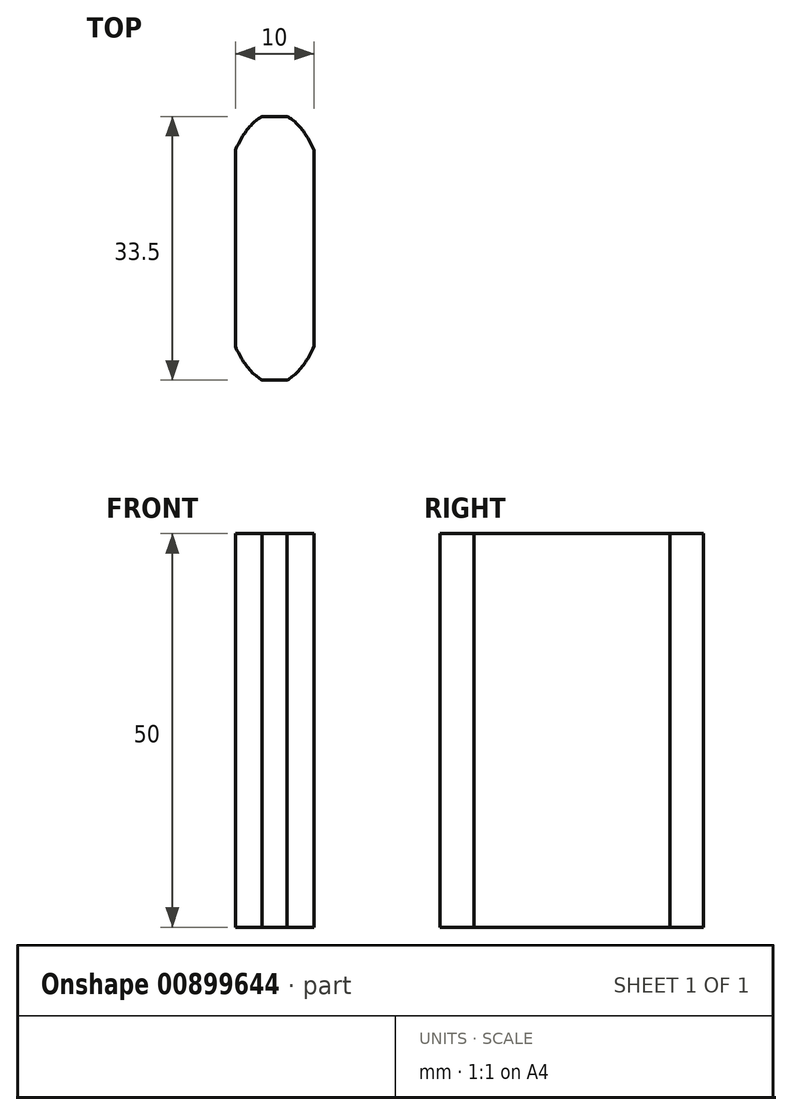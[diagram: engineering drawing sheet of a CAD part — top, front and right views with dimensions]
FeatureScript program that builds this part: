
annotation { "Feature Type Name" : "Feature", "Feature Type Description" : "" }
export const myFeature = defineFeature(function(context is Context, id is Id, definition is map)
    precondition{}
    {
        {
            var Q0;
            Q0=qCreatedBy(makeId("Right.planeOp"),FACE);
            var sketch = newSketch(context, id + "F0", { "sketchPlane" : qUnion([Q0])});
            skLineSegment(sketch, "E0.bottom", {"start": v(-36.1, 65.33) * mm, "end": v(-2.6, 65.33) * mm});
            skLineSegment(sketch, "E0.top", {"start": v(-36.1, 15.33) * mm, "end": v(-2.6, 15.33) * mm});
            skLineSegment(sketch, "E0.left", {"start": v(-36.1, 65.33) * mm, "end": v(-36.1, 15.33) * mm});
            skLineSegment(sketch, "E0.right", {"start": v(-2.6, 65.33) * mm, "end": v(-2.6, 15.33) * mm});
            skSolve(sketch);
        }
        {
            var Q0;
            Q0=makeQuery(id+"F0.imprint","IMPRINT",FACE,{"disambiguationData":[TD([[makeQuery(id+"F0.imprint","IMPRINT",EDGE,{"derivedFrom":sQuery(id+"F0.wireOp",EDGE,"E0.bottom")}),-1.0]])]});
            extrude(context, id + "F1", {"entities" : qUnion([Q0]), "depth" : 10 * mm, "offsetDistance" : 25.4 * mm});
        }
        {
            var Q0;
            Q0=makeQuery(id+"F1.opExtrude","SWEPT_FACE",FACE,{"disambiguationData":[OSD([sQuery(id+"F0.wireOp",EDGE,"E0.top")])]});
            var sketch = newSketch(context, id + "F2", { "sketchPlane" : qUnion([Q0])});
            skPoint(sketch, "E1.centerSnap0", {"position": v(5, 2.6) * mm});
            skPoint(sketch, "E1.centerSnap1", {"position": v(10, 19.34) * mm});
            skEllipticalArc(sketch, "E2", {});
            skLineSegment(sketch, "E3.bottom", {"start": v(0, 36.1) * mm, "end": v(3.42, 36.1) * mm});
            skLineSegment(sketch, "E3.top", {"start": v(0, 2.6) * mm, "end": v(3.42, 2.6) * mm});
            skLineSegment(sketch, "E3.left", {"start": v(0, 36.1) * mm, "end": v(0, 31.8) * mm});
            skLineSegment(sketch, "E3.right", {"start": v(10, 36.1) * mm, "end": v(10, 31.8) * mm});
            skEllipticalArc(sketch, "E4.trimOffspring", {});
            skEllipticalArc(sketch, "E5.trimOffspring", {});
            skEllipticalArc(sketch, "E6.trimOffspring", {});
            skLineSegment(sketch, "E7", {"start": v(0, 31.8) * mm, "end": v(0, 36.1) * mm});
            skLineSegment(sketch, "E8", {"start": v(3.42, 36.1) * mm, "end": v(0, 36.1) * mm});
            skLineSegment(sketch, "E9", {"start": v(6.58, 36.1) * mm, "end": v(10, 36.1) * mm});
            skLineSegment(sketch, "E10.trimOffspring", {"start": v(10, 6.89) * mm, "end": v(10, 2.6) * mm});
            skLineSegment(sketch, "E11.trimOffspring", {"start": v(0, 6.89) * mm, "end": v(0, 2.6) * mm});
            skLineSegment(sketch, "E12.trimOffspring", {"start": v(6.58, 2.6) * mm, "end": v(10, 2.6) * mm});
            const initialGuessF2  = {"E2": [0.005, 0.01934192111717438, 0, 1, 0.017157486025226362, 0.007270473143512162, 0.21837746983068482, 0.7583343290873897], "E4.trimOffspring": [0.005, 0.01934192111717438, 0, 1, 0.017157486025226362, 0.007270473143512162, 5.524850978092196, 6.064807837348901], "E5.trimOffspring": [0.005, 0.01934192111717438, 0, 1, 0.017157486025226362, 0.007270473143512162, 3.359970123420477, 3.899926982677181], "E6.trimOffspring": [0.005, 0.01934192111717438, 0, 1, 0.017157486025226362, 0.007270473143512162, 2.3832583245024037, 2.923215183759109]};
            skSetInitialGuess(sketch, initialGuessF2);
            skSolve(sketch);
        }
        {
            var Q0;
            Q0 = qSketchRegion(id + "F2", true);
            extrude(context, id + "F3", {"entities" : qUnion([Q0]), "operationType" : NewBodyOperationType.REMOVE, "endBound" : BoundingType.UP_TO_NEXT, "oppositeDirection" : true, "depth" : 25.4 * mm, "offsetDistance" : 25.4 * mm});
        }
    });
